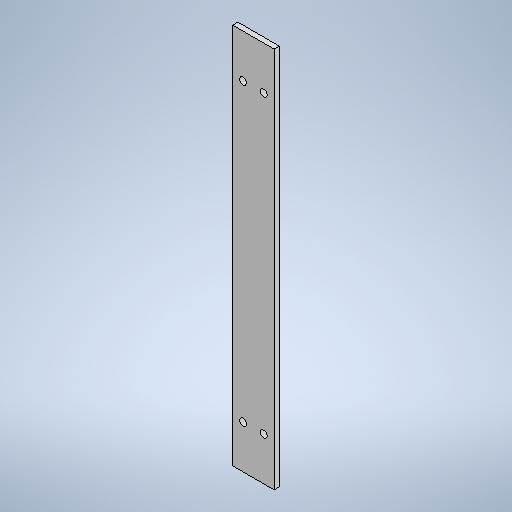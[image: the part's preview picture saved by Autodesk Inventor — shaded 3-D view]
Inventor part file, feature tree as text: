
AUTODESK INVENTOR PART (.ipt)
format: ipt  version: 2025 (Build 290162010, 162A)  size: 265,216 bytes
history: native  units: mm
features: sketch x2, extrude x1, hole x1
ambient origin geometry x8: Origin, YZ Plane, XZ Plane, XY Plane, X Axis, Y Axis, Z Axis, Center Point
bodies: Solid1 (feature_tree)
feature tree (4):
  extrude  "Extrusion1"  Depth=221.0mm
  hole  "Hole1"  [1 undecoded]
  sketch  "Sketch1"  dims[d0=24.0mm d1=221.0mm]
  sketch  "Sketch2"  dims[d2=3.0mm d3=0.0mm d4=12.0mm d5=6.0mm d6=171.0mm d7=25.0mm d8=4.0mm d9=6.0mm d10=4.0mm d11=2.0mm d12=90.0deg d13=8.0mm d14=0.0mm]
note: 1 required parameter value undecoded (feature->parameter linkage not recoverable at this tier; creation-order binding heuristic only, values carry confidence <= 0.55)
